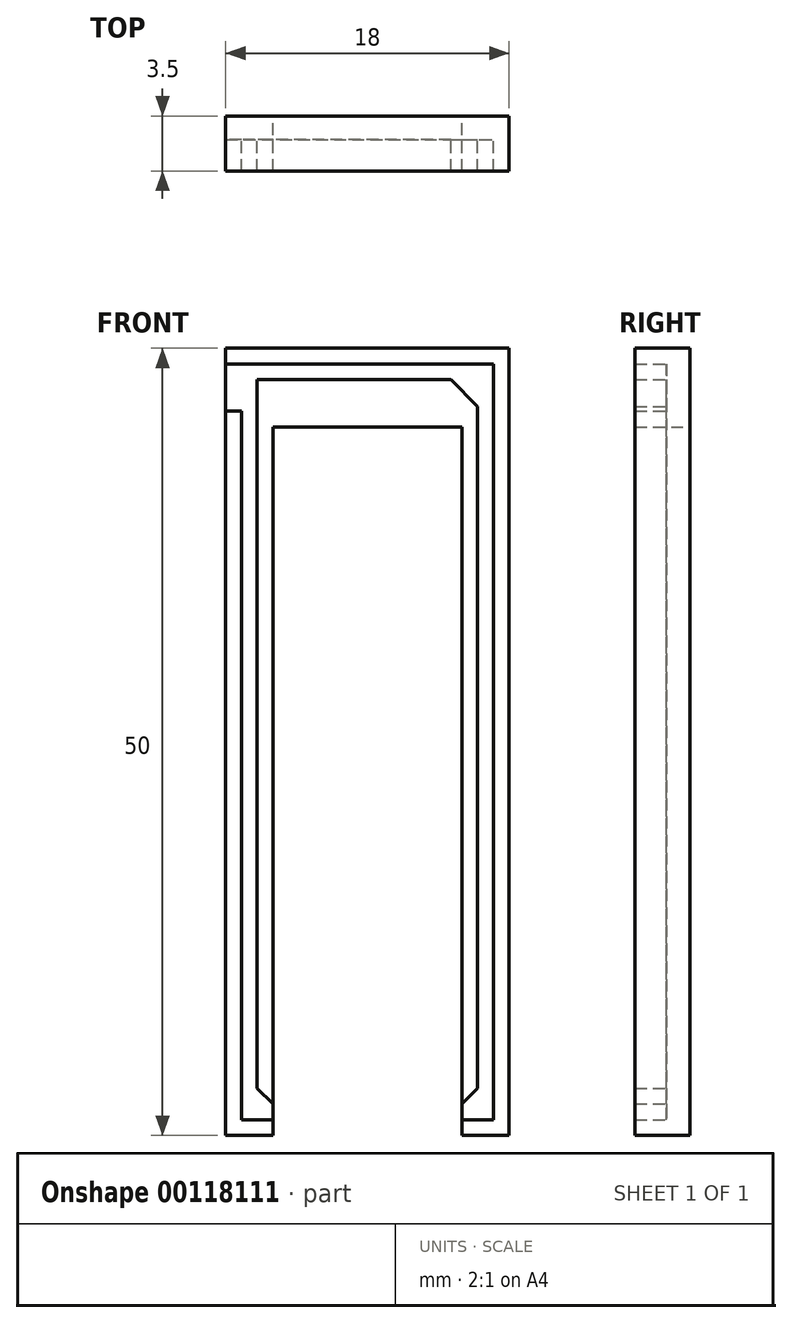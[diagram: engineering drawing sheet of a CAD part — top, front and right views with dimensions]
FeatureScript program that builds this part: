
annotation { "Feature Type Name" : "Feature", "Feature Type Description" : "" }
export const myFeature = defineFeature(function(context is Context, id is Id, definition is map)
    precondition{}
    {
        {
            var Q0;
            Q0=qCreatedBy(makeId("Front.planeOp"),FACE);
            var sketch = newSketch(context, id + "F0", { "sketchPlane" : qUnion([Q0])});
            skLineSegment(sketch, "E0", {"start": v(0, 0) * mm, "end": v(18, 0) * mm});
            skLineSegment(sketch, "E1", {"start": v(18, 0) * mm, "end": v(18, -50) * mm});
            skLineSegment(sketch, "E2", {"start": v(18, -50) * mm, "end": v(15, -50) * mm});
            skLineSegment(sketch, "E3", {"start": v(15, -50) * mm, "end": v(15, -5) * mm});
            skLineSegment(sketch, "E4", {"start": v(15, -5) * mm, "end": v(3, -5) * mm});
            skLineSegment(sketch, "E5", {"start": v(3, -5) * mm, "end": v(3, -50) * mm});
            skLineSegment(sketch, "E6", {"start": v(3, -50) * mm, "end": v(0, -50) * mm});
            skLineSegment(sketch, "E7", {"start": v(0, -50) * mm, "end": v(0, 0) * mm});
            skSolve(sketch);
        }
        {
            var Q0;
            Q0=makeQuery(id+"F0.imprint","IMPRINT",FACE,{"disambiguationData":[TD([[makeQuery(id+"F0.imprint","IMPRINT",EDGE,{"derivedFrom":sQuery(id+"F0.wireOp",EDGE,"E0")}),-1.0]])]});
            extrude(context, id + "F1", {"entities" : qUnion([Q0]), "depth" : 1.5 * mm});
        }
        {
            var Q0;
            Q0=makeQuery(id+"F1.opExtrude","CAP_FACE",FACE,{"disambiguationData":[OSD([sQuery(id+"F0.wireOp",EDGE,"E0"),sQuery(id+"F0.wireOp",EDGE,"E1"),sQuery(id+"F0.wireOp",EDGE,"E2"),sQuery(id+"F0.wireOp",EDGE,"E3"),sQuery(id+"F0.wireOp",EDGE,"E4"),sQuery(id+"F0.wireOp",EDGE,"E5"),sQuery(id+"F0.wireOp",EDGE,"E6"),sQuery(id+"F0.wireOp",EDGE,"E7")])],"isStart":false});
            var sketch = newSketch(context, id + "F2", { "sketchPlane" : qUnion([Q0])});
            skLineSegment(sketch, "E8", {"start": v(0, -1) * mm, "end": v(17, -1) * mm});
            skLineSegment(sketch, "E9", {"start": v(17, -1) * mm, "end": v(17, -49) * mm});
            skLineSegment(sketch, "E10", {"start": v(15, -49) * mm, "end": v(17, -49) * mm});
            skLineSegment(sketch, "E11", {"start": v(15, -48) * mm, "end": v(16, -47) * mm});
            skLineSegment(sketch, "E12", {"start": v(16, -47) * mm, "end": v(16, -3.7) * mm});
            skLineSegment(sketch, "E13", {"start": v(14.3, -2) * mm, "end": v(2, -2) * mm});
            skPoint(sketch, "E14.orphan", {"position": v(17, -50) * mm});
            skLineSegment(sketch, "E15", {"start": v(3, -49) * mm, "end": v(1, -49) * mm});
            skLineSegment(sketch, "E16", {"start": v(1, -49) * mm, "end": v(1, -4) * mm});
            skLineSegment(sketch, "E17", {"start": v(1, -4) * mm, "end": v(0, -4) * mm});
            skLineSegment(sketch, "E18", {"start": v(3, -48) * mm, "end": v(2, -47) * mm});
            skLineSegment(sketch, "E19", {"start": v(2, -47) * mm, "end": v(2, -4.21) * mm});
            skLineSegment(sketch, "E20", {"start": v(2, -4.21) * mm, "end": v(2, -2) * mm});
            skPoint(sketch, "E21.orphan", {"position": v(0, -2) * mm});
            skLineSegment(sketch, "E22", {"start": v(14.3, -2) * mm, "end": v(16, -3.7) * mm});
            skSolve(sketch);
        }
        {
            var Q0;
            {var subQ3=sQuery(id+"F2.wireOp",EDGE,"E8");Q0=makeQuery(id+"F2.imprint","IMPRINT",FACE,{"disambiguationData":[TD([[makeQuery(id+"F2.imprint","IMPRINT",EDGE,{"derivedFrom":subQ3}),1.0]])]});}
            var Q1;
            {var subQ1=sQuery(id+"F2.wireOp",EDGE,"E11");Q1=makeQuery(id+"F2.imprint","IMPRINT",FACE,{"disambiguationData":[TD([[makeQuery(id+"F2.imprint","IMPRINT",EDGE,{"derivedFrom":subQ1}),1.0]])]});}
            var Q2;
            {var subQ3=sQuery(id+"F2.wireOp",EDGE,"E15");Q2=makeQuery(id+"F2.imprint","IMPRINT",FACE,{"disambiguationData":[TD([[makeQuery(id+"F2.imprint","IMPRINT",EDGE,{"derivedFrom":subQ3}),1.0]])]});}
            extrude(context, id + "F3", {"entities" : qUnion([Q0, Q1, Q2]), "operationType" : NewBodyOperationType.ADD, "depth" : 2 * mm});
        }
    });
